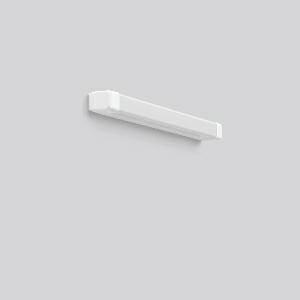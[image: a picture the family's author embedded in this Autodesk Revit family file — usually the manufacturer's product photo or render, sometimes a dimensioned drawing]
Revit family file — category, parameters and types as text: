
# Revit family: baleva_451201_002_2_4d42
name_source: partatom
category: Lighting Fixtures
units: mm (PartAtom-declared; Revit-internal decimal feet)

## family parameters
Cut with Voids When Loaded = No
Host = Face
Light Source = No
Part Type = Normal
Room Calculation Point = No
Round Connector Dimension = Use Diameter
Shared = No

## types (1)
- MultiColor 830 (1 x LED Modul 830, 1050 lm, 3000)
    Apparent Load = 10 VA
    CIE Flux Codes = 40 69 88 82 100
    Color Rendering = 80
    Color Temperature = 3000
    Default Elevation = 1800 mm
    Description = Series: BALEVA
Linear luminaire with timeless functional design. Ideal for sanitary areas, corridors, waiting areas, nursing homes, patient rooms. Body and end caps made of white plastic. Diffuser made of plastic (polycarbonate), opal, shockproof. Homogeneous and smooth light distribution. MultiColour: With rear switching element, variable colour temperature 3000  K or 4000  K. Factory setting is 4000 K. Diffuser can be assembled without the use of tools. Quick and easy to install. Can be installed horizontally and vertically. 2 central cable inlets for looping the cable. Converter integrated and encapsulated. 
Colour: white
Length: 600 mm
Width: 46 mm
Height: 60 mm
Lamp: LED
Socket: without socket
Colour temperature: 3000K, 4000K
Colour rendering index (CRI): 80
System power: 10 W
Rated luminous flux: 1050 lm
Luminous efficiency: 105 lm/W
System power 2: 10 W
Rated luminous flux 2: 1100 lm
Luminous efficiency 2: 110 lm/W
Control gear: Regulated power supply
Protection class: II
Type of protection: IP 40
    Height = 60 mm  [stored 0.19685 ft]
    Lamp = 1 x LED Modul 830
    Lamp Light Flux = 1050 lm
    Lamp count = 1
    Length = 600 mm
    Lifetime = 50000 h
    Luminous efficacy = 105 lm/W
    Manufacturer = RZB
    ModVariant = No
    Model = 451201.002.2
    Mounting Place = Ceiling, Wall
    Mounting Type = Surface mounted
    Number of Poles = 1
    OnlyDefault = Yes
    Power Factor = 1
    Product Name = BALEVA
    Product group = Surface mounted ceiling and wall luminaires
    ProductGroupID = 305
    Protection Class = Protection class II
    Protection Degree = IP 40
    RLX_Detail_Level = 1
    RLX_Emergency_Light_Flux = 0 lm
    RLX_Emergency_Type = 0
    RLX_Emergency_Type_DB = No
    RlxData = <blob elided: 38633 chars, md5=8404a254>
    Socket = socket
    Standby Power = 0 W
    System Light Flux = 1050 lm
    System Power = 10 W
    Type Comments = MultiColor 830
    Type Image = 451201.002.jpg
    URL = http://relux.com
    VarID = multicolor_830
    Voltage = 230 V
    Voltage Range = 220-240 V
    Weight = 0.00 kg
    Width = 46 mm

note: [stored X ft] marks values corroborated as IEEE doubles in the binary element streams (Revit-internal decimal feet)

## geometry (parser evidence)
native form markers: Blend x4, Sweep x13
no freeform markers — native parametric forms only
